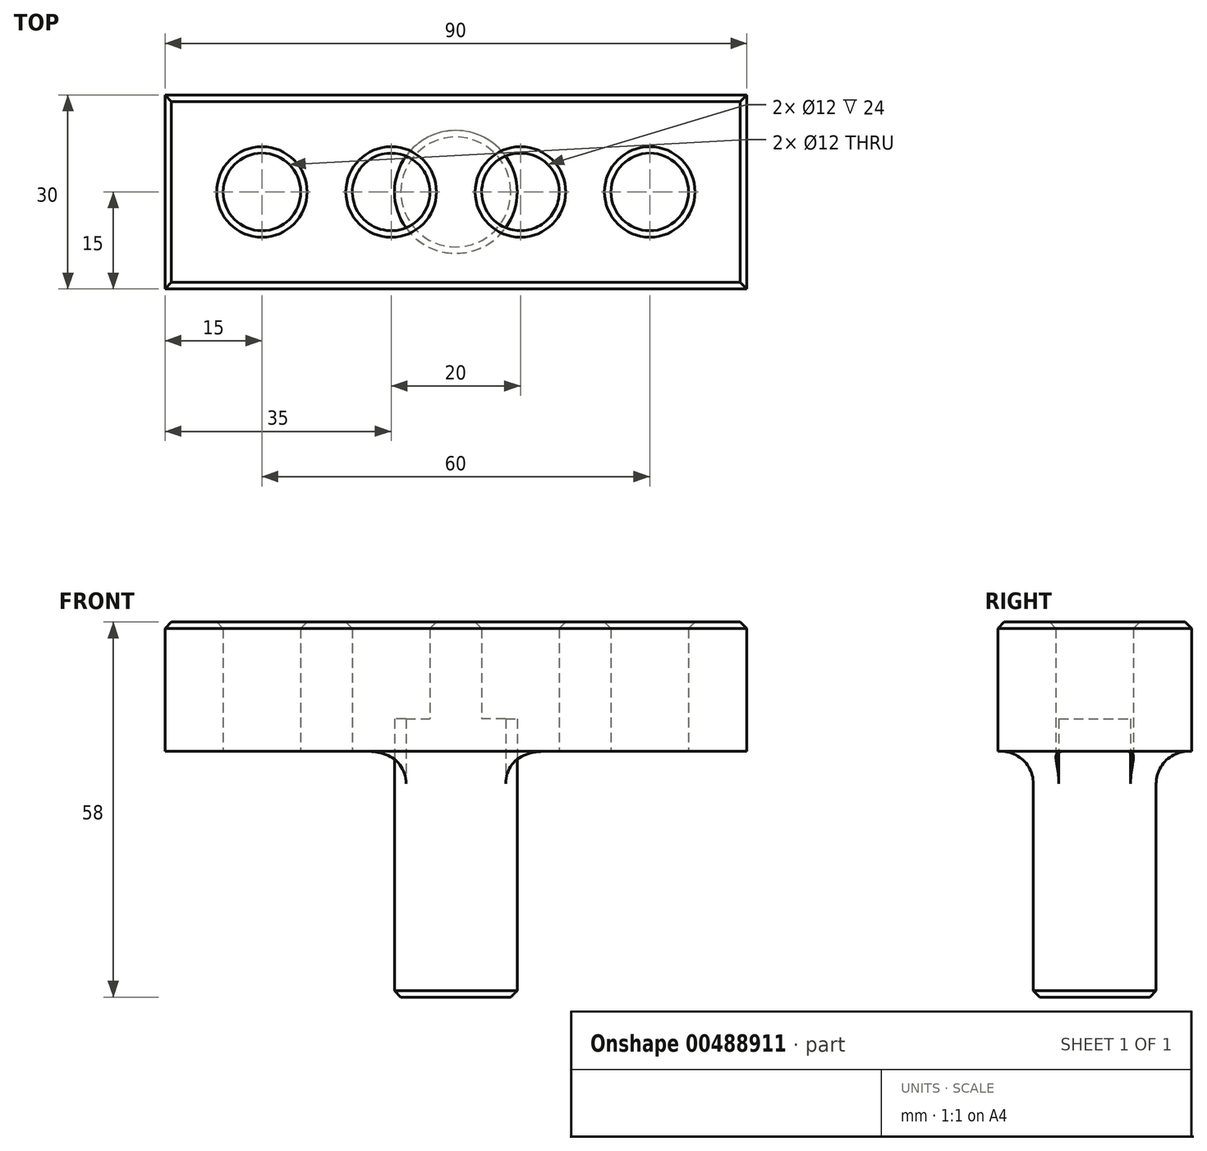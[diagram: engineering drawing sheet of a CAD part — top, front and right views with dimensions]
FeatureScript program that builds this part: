
annotation { "Feature Type Name" : "Feature", "Feature Type Description" : "" }
export const myFeature = defineFeature(function(context is Context, id is Id, definition is map)
    precondition{}
    {
        {
            var Q0;
            Q0=qCreatedBy(makeId("Top.planeOp"),FACE);
            var sketch = newSketch(context, id + "F0", { "sketchPlane" : qUnion([Q0])});
            skLineSegment(sketch, "E0.bottom", {"start": v(-45, 15) * mm, "end": v(45, 15) * mm});
            skLineSegment(sketch, "E0.top", {"start": v(-45, -15) * mm, "end": v(45, -15) * mm});
            skLineSegment(sketch, "E0.left", {"start": v(-45, 15) * mm, "end": v(-45, -15) * mm});
            skLineSegment(sketch, "E0.right", {"start": v(45, 15) * mm, "end": v(45, -15) * mm});
            skPoint(sketch, "E0.middle", {"position": v(0, 0) * mm});
            skLineSegment(sketch, "E1", {"start": v(-45, -15) * mm, "end": v(-45, 0) * mm, "construction": true});
            skLineSegment(sketch, "E2", {"start": v(-45, 0) * mm, "end": v(45, 0) * mm, "construction": true});
            skLineSegment(sketch, "E3", {"start": v(45, 0) * mm, "end": v(45, 10) * mm, "construction": true});
            skLineSegment(sketch, "E4", {"start": v(45, 10) * mm, "end": v(-127.47, 10) * mm, "construction": true});
            skLineSegment(sketch, "E5", {"start": v(-45, 0) * mm, "end": v(-30, 0) * mm, "construction": true});
            skLineSegment(sketch, "E6", {"start": v(-30, 0) * mm, "end": v(-30, -10) * mm, "construction": true});
            skCircle(sketch, "E7", {"center": v(-30, 0) * mm, "radius": 6 * mm});
            skCircle(sketch, "E8.1.0.0", {"center": v(-10, 0) * mm, "radius": 6 * mm});
            skCircle(sketch, "E8.2.0.0", {"center": v(10, 0) * mm, "radius": 6 * mm});
            skCircle(sketch, "E8.3.0.0", {"center": v(30, 0) * mm, "radius": 6 * mm});
            skLineSegment(sketch, "E8.direction1", {"start": v(-30, 0) * mm, "end": v(-10, 0) * mm, "construction": true});
            skSolve(sketch);
        }
        {
            var Q0;
            Q0=makeQuery(id+"F0.imprint","IMPRINT",FACE,{"disambiguationData":[TD([[makeQuery(id+"F0.imprint","IMPRINT",EDGE,{"derivedFrom":sQuery(id+"F0.wireOp",EDGE,"E0.bottom")}),-1.0]])]});
            extrude(context, id + "F1", {"entities" : qUnion([Q0]), "depth" : 20 * mm});
        }
        {
            var Q0;
            Q0=makeQuery(id+"F1.opExtrude","CAP_FACE",FACE,{"disambiguationData":[OSD([sQuery(id+"F0.wireOp",EDGE,"E0.bottom"),sQuery(id+"F0.wireOp",EDGE,"E0.top"),sQuery(id+"F0.wireOp",EDGE,"E0.left"),sQuery(id+"F0.wireOp",EDGE,"E0.right"),sQuery(id+"F0.wireOp",EDGE,"E7"),sQuery(id+"F0.wireOp",EDGE,"E8.1.0.0"),sQuery(id+"F0.wireOp",EDGE,"E8.2.0.0"),sQuery(id+"F0.wireOp",EDGE,"E8.3.0.0"),sQuery(id+"F0.wireOp",EDGE,"E8.4.0.0"),sQuery(id+"F0.wireOp",EDGE,"E8.5.0.0"),sQuery(id+"F0.wireOp",EDGE,"E8.6.0.0"),sQuery(id+"F0.wireOp",EDGE,"E8.7.0.0"),sQuery(id+"F0.wireOp",EDGE,"E8.8.0.0"),sQuery(id+"F0.wireOp",EDGE,"E8.9.0.0"),sQuery(id+"F0.wireOp",EDGE,"E8.10.0.0"),sQuery(id+"F0.wireOp",EDGE,"E8.11.0.0")])],"isStart":false});
            chamfer(context, id + "F2", {"entities" : qUnion([Q0]), "width" : 1 * mm, "tangentPropagation" : true});
        }
        {
            var Q0;
            Q0=qCreatedBy(makeId("Top.planeOp"),FACE);
            var sketch = newSketch(context, id + "F3", { "sketchPlane" : qUnion([Q0])});
            skCircle(sketch, "E9", {"center": v(0, 0) * mm, "radius": 9.5 * mm});
            skSolve(sketch);
        }
        {
            var Q0;
            Q0 = qSketchRegion(id + "F3", true);
            extrude(context, id + "F4", {"entities" : qUnion([Q0]), "operationType" : NewBodyOperationType.ADD, "depth" : 5 * mm, "hasSecondDirection" : true, "secondDirectionOppositeDirection" : true, "secondDirectionDepth" : 38 * mm});
        }
        {
            var Q0;
            Q0=makeQuery(id+"F4.opExtrude","CAP_EDGE",EDGE,{"disambiguationData":[OSD([sQuery(id+"F3.wireOp",EDGE,"E9")])],"isStart":true});
            chamfer(context, id + "F5", {"entities" : qUnion([Q0]), "width" : 1 * mm, "tangentPropagation" : true});
        }
        {
            var Q0;
            Q0=makeQuery(id+"F4.boolean.opBoolean","INTERSECT",EDGE,{"disambiguationData":[OD(0.0)],"derivedFrom":[makeQuery(id+"F1.opExtrude","CAP_FACE",FACE,{"disambiguationData":[OSD([sQuery(id+"F0.wireOp",EDGE,"E0.bottom"),sQuery(id+"F0.wireOp",EDGE,"E0.top"),sQuery(id+"F0.wireOp",EDGE,"E0.left"),sQuery(id+"F0.wireOp",EDGE,"E0.right"),sQuery(id+"F0.wireOp",EDGE,"E7"),sQuery(id+"F0.wireOp",EDGE,"E8.1.0.0"),sQuery(id+"F0.wireOp",EDGE,"E8.2.0.0"),sQuery(id+"F0.wireOp",EDGE,"E8.3.0.0"),sQuery(id+"F0.wireOp",EDGE,"E8.4.0.0"),sQuery(id+"F0.wireOp",EDGE,"E8.5.0.0"),sQuery(id+"F0.wireOp",EDGE,"E8.6.0.0"),sQuery(id+"F0.wireOp",EDGE,"E8.7.0.0"),sQuery(id+"F0.wireOp",EDGE,"E8.8.0.0"),sQuery(id+"F0.wireOp",EDGE,"E8.9.0.0"),sQuery(id+"F0.wireOp",EDGE,"E8.10.0.0"),sQuery(id+"F0.wireOp",EDGE,"E8.11.0.0")])],"isStart":true}),makeQuery(id+"F4.opExtrude","SWEPT_FACE",FACE,{"disambiguationData":[OSD([sQuery(id+"F3.wireOp",EDGE,"E9")])]})]});
            var Q1;
            Q1=makeQuery(id+"F4.boolean.opBoolean","INTERSECT",EDGE,{"disambiguationData":[OD(1.0)],"derivedFrom":[makeQuery(id+"F1.opExtrude","CAP_FACE",FACE,{"disambiguationData":[OSD([sQuery(id+"F0.wireOp",EDGE,"E0.bottom"),sQuery(id+"F0.wireOp",EDGE,"E0.top"),sQuery(id+"F0.wireOp",EDGE,"E0.left"),sQuery(id+"F0.wireOp",EDGE,"E0.right"),sQuery(id+"F0.wireOp",EDGE,"E7"),sQuery(id+"F0.wireOp",EDGE,"E8.1.0.0"),sQuery(id+"F0.wireOp",EDGE,"E8.2.0.0"),sQuery(id+"F0.wireOp",EDGE,"E8.3.0.0"),sQuery(id+"F0.wireOp",EDGE,"E8.4.0.0"),sQuery(id+"F0.wireOp",EDGE,"E8.5.0.0"),sQuery(id+"F0.wireOp",EDGE,"E8.6.0.0"),sQuery(id+"F0.wireOp",EDGE,"E8.7.0.0"),sQuery(id+"F0.wireOp",EDGE,"E8.8.0.0"),sQuery(id+"F0.wireOp",EDGE,"E8.9.0.0"),sQuery(id+"F0.wireOp",EDGE,"E8.10.0.0"),sQuery(id+"F0.wireOp",EDGE,"E8.11.0.0")])],"isStart":true}),makeQuery(id+"F4.opExtrude","SWEPT_FACE",FACE,{"disambiguationData":[OSD([sQuery(id+"F3.wireOp",EDGE,"E9")])]})]});
            fillet(context, id + "F6", {"entities" : qUnion([Q0, Q1]), "radius" : 5 * mm, "tangentPropagation" : true, "allowEdgeOverflow" : false});
        }
    });
